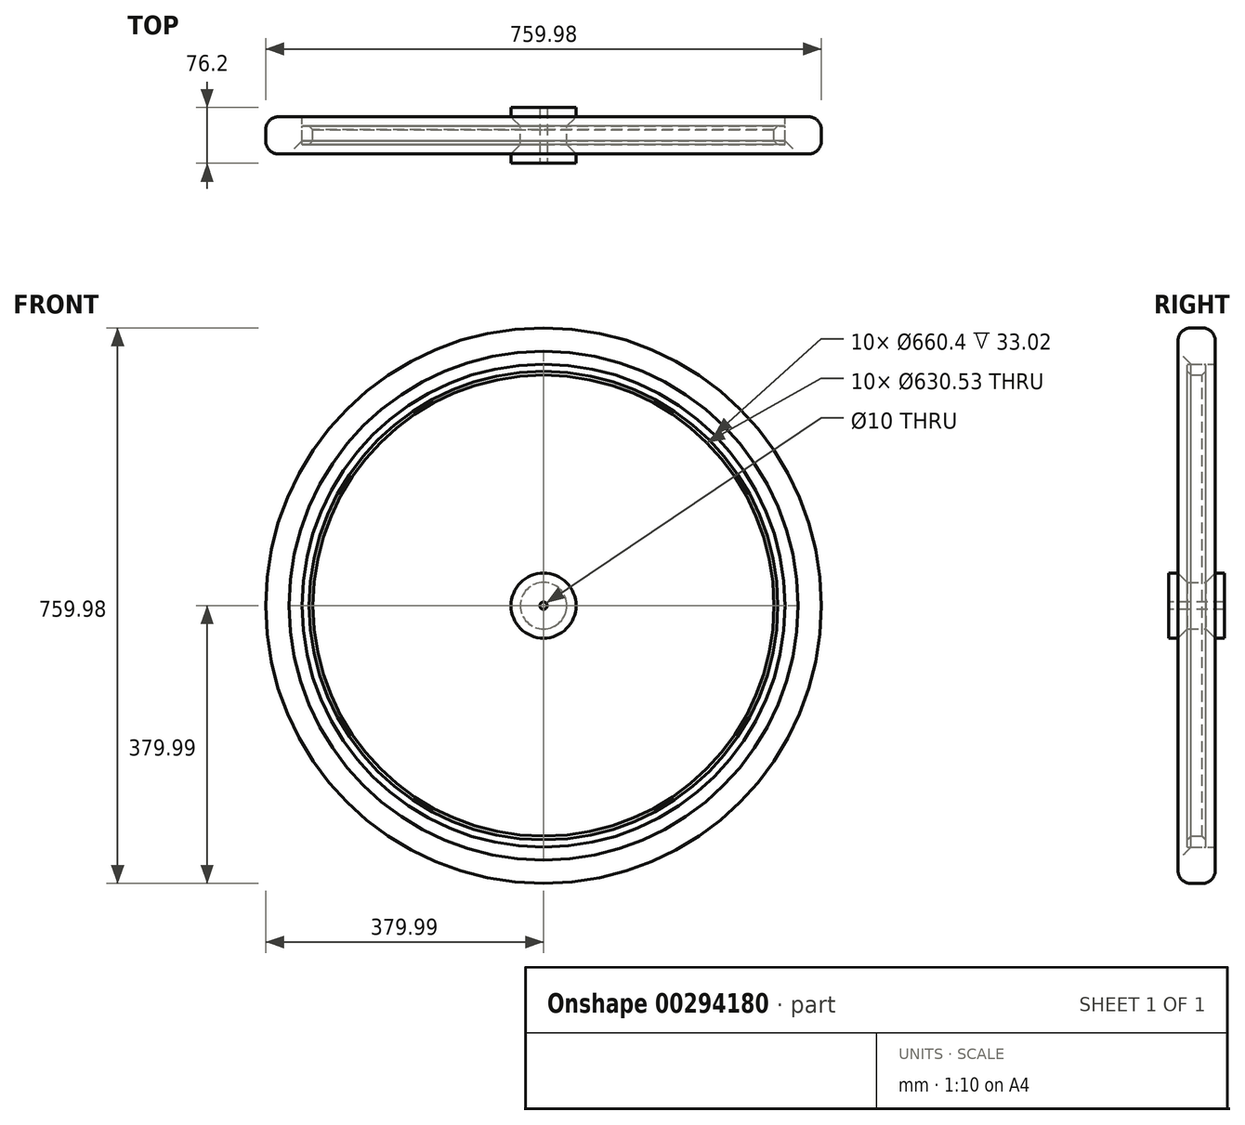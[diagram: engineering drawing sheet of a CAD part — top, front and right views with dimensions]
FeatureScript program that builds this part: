
annotation { "Feature Type Name" : "Feature", "Feature Type Description" : "" }
export const myFeature = defineFeature(function(context is Context, id is Id, definition is map)
    precondition{}
    {
        {
            var Q0;
            Q0=qCreatedBy(makeId("Front.planeOp"),FACE);
            var sketch = newSketch(context, id + "F0", { "sketchPlane" : qUnion([Q0])});
            skCircle(sketch, "E0", {"center": v(0, 0) * mm, "radius": 330.2 * mm});
            skCircle(sketch, "E1", {"center": v(0, 0) * mm, "radius": 315.27 * mm});
            skSolve(sketch);
        }
        {
            var Q0;
            Q0 = qSketchRegion(id + "F0", true);
            extrude(context, id + "F1", {"entities" : qUnion([Q0]), "endBound" : BoundingType.SYMMETRIC, "depth" : 25.4 * mm});
        }
        {
            var Q0;
            Q0=makeQuery(id+"F1.opExtrude","CAP_EDGE",EDGE,{"disambiguationData":[OSD([sQuery(id+"F0.wireOp",EDGE,"E1")])],"isStart":false});
            var Q1;
            Q1=makeQuery(id+"F1.opExtrude","CAP_EDGE",EDGE,{"disambiguationData":[OSD([sQuery(id+"F0.wireOp",EDGE,"E1")])],"isStart":true});
            chamfer(context, id + "F2", {"entities" : qUnion([Q0, Q1]), "width" : 5.08 * mm, "tangentPropagation" : true});
        }
        {
            var Q0;
            Q0=qCreatedBy(makeId("Front.planeOp"),FACE);
            var sketch = newSketch(context, id + "F3", { "sketchPlane" : qUnion([Q0])});
            skCircle(sketch, "E2", {"center": v(0, 0) * mm, "radius": 31.75 * mm});
            skSolve(sketch);
        }
        {
            var Q0;
            Q0 = qSketchRegion(id + "F3", true);
            extrude(context, id + "F4", {"entities" : qUnion([Q0]), "endBound" : BoundingType.SYMMETRIC, "depth" : 25.4 * mm});
        }
        {
            var Q0;
            Q0=makeQuery(id+"F4.opExtrude","CAP_FACE",FACE,{"disambiguationData":[OSD([sQuery(id+"F3.wireOp",EDGE,"E2")])],"isStart":false});
            var sketch = newSketch(context, id + "F5", { "sketchPlane" : qUnion([Q0])});
            skCircle(sketch, "E3", {"center": v(0, 0) * mm, "radius": 44.45 * mm});
            skSolve(sketch);
        }
        {
            var Q0;
            Q0 = qSketchRegion(id + "F5", true);
            extrude(context, id + "F6", {"entities" : qUnion([Q0]), "operationType" : NewBodyOperationType.ADD, "depth" : 25.4 * mm});
        }
        {
            var Q0;
            Q0=makeQuery(id+"F4.opExtrude","CAP_FACE",FACE,{"disambiguationData":[OSD([sQuery(id+"F3.wireOp",EDGE,"E2")])],"isStart":true});
            var sketch = newSketch(context, id + "F7", { "sketchPlane" : qUnion([Q0])});
            skCircle(sketch, "E4", {"center": v(0, 0) * mm, "radius": 44.45 * mm});
            skSolve(sketch);
        }
        {
            var Q0;
            Q0 = qSketchRegion(id + "F7", true);
            extrude(context, id + "F8", {"entities" : qUnion([Q0]), "operationType" : NewBodyOperationType.ADD, "depth" : 25.4 * mm});
        }
        {
            var Q0;
            Q0=makeQuery(id+"F6.opExtrude","CAP_EDGE",EDGE,{"disambiguationData":[OSD([sQuery(id+"F5.wireOp",EDGE,"E3")])],"isStart":true});
            var Q1;
            Q1=makeQuery(id+"F8.opExtrude","CAP_EDGE",EDGE,{"disambiguationData":[OSD([sQuery(id+"F7.wireOp",EDGE,"E4")])],"isStart":true});
            chamfer(context, id + "F9", {"entities" : qUnion([Q0, Q1]), "width" : 12.7 * mm, "tangentPropagation" : true});
        }
        {
            var Q0;
            Q0=makeQuery(id+"F6.opExtrude","CAP_FACE",FACE,{"disambiguationData":[OSD([sQuery(id+"F5.wireOp",EDGE,"E3")])],"isStart":false});
            var sketch = newSketch(context, id + "F10", { "sketchPlane" : qUnion([Q0])});
            skCircle(sketch, "E5", {"center": v(0, 0) * mm, "radius": 5 * mm});
            skSolve(sketch);
        }
        {
            var Q0;
            Q0 = qSketchRegion(id + "F10", true);
            extrude(context, id + "F11", {"entities" : qUnion([Q0]), "operationType" : NewBodyOperationType.REMOVE, "oppositeDirection" : true, "depth" : 101.6 * mm});
        }
        {
            var Q0;
            Q0=qCreatedBy(makeId("Front.planeOp"),FACE);
            var sketch = newSketch(context, id + "F12", { "sketchPlane" : qUnion([Q0])});
            skCircle(sketch, "E6", {"center": v(0, 0) * mm, "radius": 330.2 * mm});
            skCircle(sketch, "E7", {"center": v(0, 0) * mm, "radius": 379.99 * mm});
            skSolve(sketch);
        }
        {
            var Q0;
            Q0 = qSketchRegion(id + "F12", true);
            extrude(context, id + "F13", {"entities" : qUnion([Q0]), "endBound" : BoundingType.SYMMETRIC, "depth" : 50.8 * mm});
        }
        {
            var Q0;
            Q0=makeQuery(id+"F13.opExtrude","CAP_EDGE",EDGE,{"disambiguationData":[OSD([sQuery(id+"F12.wireOp",EDGE,"E6")])],"isStart":false});
            chamfer(context, id + "F14", {"entities" : qUnion([Q0]), "width" : 17.78 * mm, "tangentPropagation" : true});
        }
        {
            var Q0;
            Q0=makeQuery(id+"F13.opExtrude","CAP_EDGE",EDGE,{"disambiguationData":[OSD([sQuery(id+"F12.wireOp",EDGE,"E7")])],"isStart":false});
            var Q1;
            Q1=makeQuery(id+"F13.opExtrude","CAP_EDGE",EDGE,{"disambiguationData":[OSD([sQuery(id+"F12.wireOp",EDGE,"E7")])],"isStart":true});
            fillet(context, id + "F15", {"entities" : qUnion([Q0, Q1]), "radius" : 17.78 * mm, "tangentPropagation" : true, "allowEdgeOverflow" : false});
        }
    });
